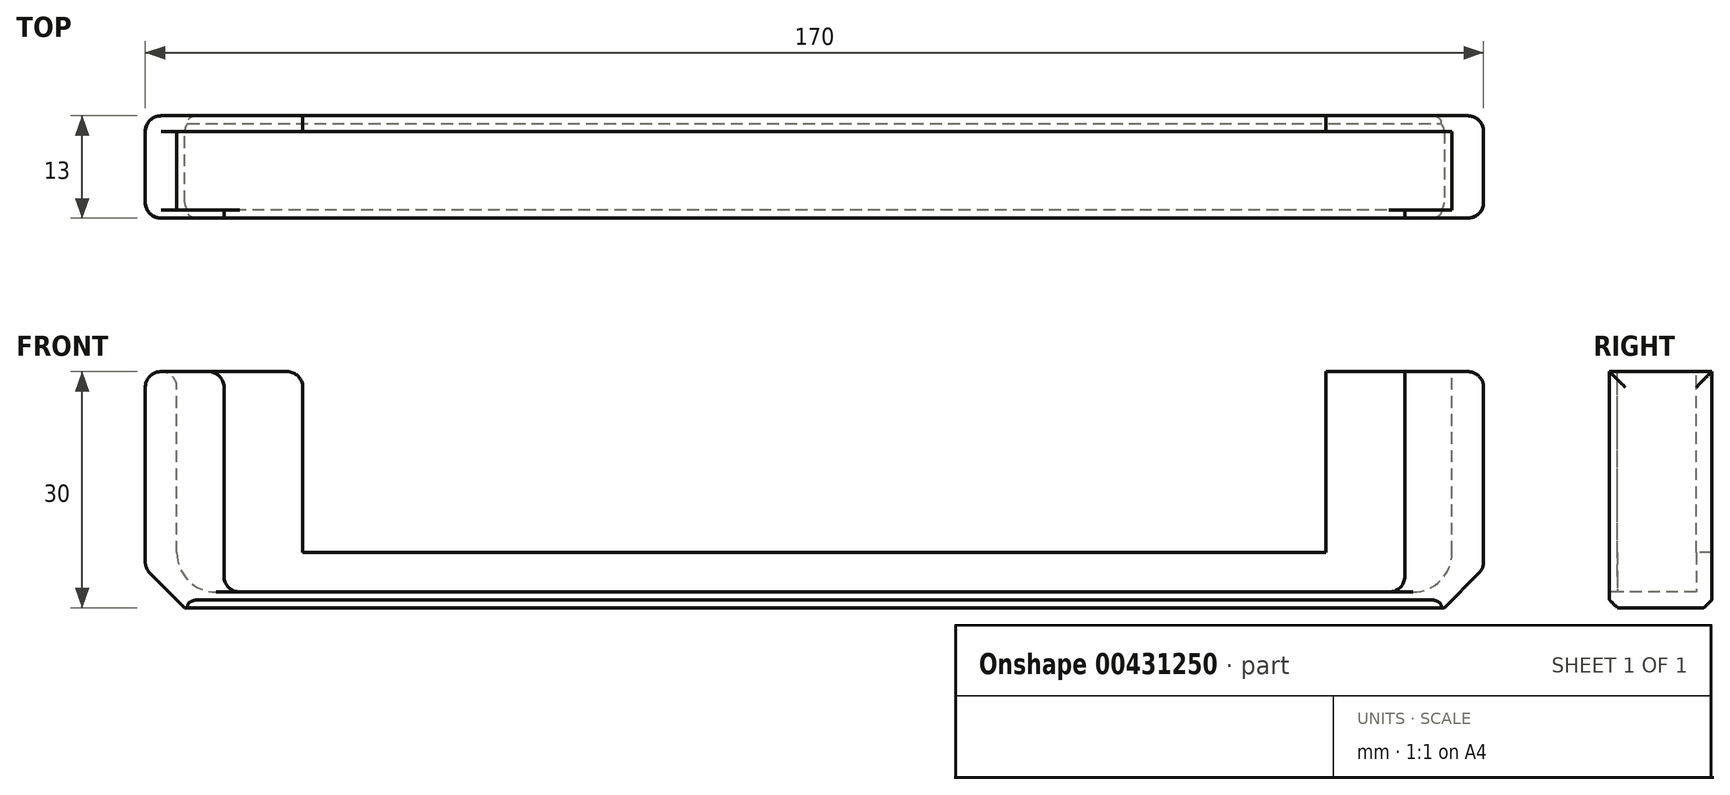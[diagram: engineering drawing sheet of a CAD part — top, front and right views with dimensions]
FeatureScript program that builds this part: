
annotation { "Feature Type Name" : "Feature", "Feature Type Description" : "" }
export const myFeature = defineFeature(function(context is Context, id is Id, definition is map)
    precondition{}
    {
        {
            var Q0;
            Q0=qCreatedBy(makeId("Front.planeOp"),FACE);
            var sketch = newSketch(context, id + "F0", { "sketchPlane" : qUnion([Q0])});
            skLineSegment(sketch, "E0.bottom", {"start": v(-85, 0) * mm, "end": v(85, 0) * mm});
            skLineSegment(sketch, "E0.top", {"start": v(-85, 30) * mm, "end": v(85, 30) * mm});
            skLineSegment(sketch, "E0.left", {"start": v(-85, 0) * mm, "end": v(-85, 30) * mm});
            skLineSegment(sketch, "E0.right", {"start": v(85, 0) * mm, "end": v(85, 30) * mm});
            skSolve(sketch);
        }
        {
            var Q0;
            Q0=qSketchRegion(id+"F0",true);
            extrude(context, id + "F1", {"entities" : qUnion([Q0]), "depth" : 13 * mm});
        }
        {
            var Q0;
            Q0=makeQuery(id+"F1.opExtrude","SWEPT_FACE",FACE,{"disambiguationData":[OSD([sQuery(id+"F0.wireOp",EDGE,"E0.top")])]});
            var sketch = newSketch(context, id + "F2", { "sketchPlane" : qUnion([Q0])});
            skLineSegment(sketch, "E1.bottom", {"start": v(-81, -2) * mm, "end": v(-65, -2) * mm});
            skLineSegment(sketch, "E1.top", {"start": v(-81, -12) * mm, "end": v(-75, -12) * mm});
            skLineSegment(sketch, "E1.left", {"start": v(-81, -2) * mm, "end": v(-81, -12) * mm});
            skLineSegment(sketch, "E1.right", {"start": v(81, -2) * mm, "end": v(81, -12) * mm});
            skLineSegment(sketch, "E2", {"start": v(-75, -12) * mm, "end": v(-75, -13) * mm});
            skLineSegment(sketch, "E3", {"start": v(-75, -13) * mm, "end": v(75, -13) * mm});
            skLineSegment(sketch, "E4", {"start": v(75, -13) * mm, "end": v(75, -12) * mm});
            skLineSegment(sketch, "E5.trimOffspring", {"start": v(75, -12) * mm, "end": v(81, -12) * mm});
            skLineSegment(sketch, "E6", {"start": v(-65, -2) * mm, "end": v(-65, 0) * mm});
            skLineSegment(sketch, "E7", {"start": v(-65, 0) * mm, "end": v(65, 0) * mm});
            skLineSegment(sketch, "E8", {"start": v(65, 0) * mm, "end": v(65, -2) * mm});
            skLineSegment(sketch, "E9.trimOffspring", {"start": v(65, -2) * mm, "end": v(81, -2) * mm});
            skSolve(sketch);
        }
        {
            var Q0;
            Q0=qSketchRegion(id+"F2",true);
            extrude(context, id + "F3", {"entities" : qUnion([Q0]), "operationType" : NewBodyOperationType.REMOVE, "oppositeDirection" : true, "depth" : 28 * mm});
        }
        {
            var Q0;
            Q0=makeQuery(id+"F3.boolean.opBoolean","COPY",FACE,{"derivedFrom":makeQuery(id+"F3.opExtrude","CAP_FACE",FACE,{"disambiguationData":[OSD([sQuery(id+"F2.wireOp",EDGE,"E1.bottom"),sQuery(id+"F2.wireOp",EDGE,"E1.top"),sQuery(id+"F2.wireOp",EDGE,"E1.left"),sQuery(id+"F2.wireOp",EDGE,"E1.right"),sQuery(id+"F2.wireOp",EDGE,"E2"),sQuery(id+"F2.wireOp",EDGE,"E3"),sQuery(id+"F2.wireOp",EDGE,"E4"),sQuery(id+"F2.wireOp",EDGE,"E5.trimOffspring"),sQuery(id+"F2.wireOp",EDGE,"E6"),sQuery(id+"F2.wireOp",EDGE,"E7"),sQuery(id+"F2.wireOp",EDGE,"E8"),sQuery(id+"F2.wireOp",EDGE,"E9.trimOffspring")])],"isStart":false})});
            var sketch = newSketch(context, id + "F4", { "sketchPlane" : qUnion([Q0])});
            skLineSegment(sketch, "E10.bottom", {"start": v(65, -2) * mm, "end": v(-65, -2) * mm});
            skLineSegment(sketch, "E10.top", {"start": v(65, 0) * mm, "end": v(-65, 0) * mm});
            skLineSegment(sketch, "E10.left", {"start": v(65, -2) * mm, "end": v(65, 0) * mm});
            skLineSegment(sketch, "E10.right", {"start": v(-65, -2) * mm, "end": v(-65, 0) * mm});
            skSolve(sketch);
        }
        {
            var Q0;
            Q0=qSketchRegion(id+"F4",true);
            extrude(context, id + "F5", {"entities" : qUnion([Q0]), "operationType" : NewBodyOperationType.ADD, "depth" : 5 * mm});
        }
        {
            var Q0;
            Q0=makeQuery(id+"F1.opExtrude","SWEPT_EDGE",EDGE,{"disambiguationData":[OSD([sQuery(id+"F0.wireOp",EDGE,"E0.bottom"),sQuery(id+"F0.wireOp",EDGE,"E0.right")])]});
            var Q1;
            Q1=makeQuery(id+"F1.opExtrude","SWEPT_EDGE",EDGE,{"disambiguationData":[OSD([sQuery(id+"F0.wireOp",EDGE,"E0.bottom"),sQuery(id+"F0.wireOp",EDGE,"E0.left")])]});
            chamfer(context, id + "F6", {"entities" : qUnion([Q0, Q1]), "width" : 5 * mm, "tangentPropagation" : true});
        }
        {
            var Q0;
            Q0=makeQuery(id+"F3.boolean.opBoolean","COPY",EDGE,{"derivedFrom":makeQuery(id+"F3.opExtrude","CAP_EDGE",EDGE,{"disambiguationData":[OSD([sQuery(id+"F2.wireOp",EDGE,"E1.left")])],"isStart":false})});
            var Q1;
            Q1=makeQuery(id+"F3.boolean.opBoolean","COPY",EDGE,{"derivedFrom":makeQuery(id+"F3.opExtrude","CAP_EDGE",EDGE,{"disambiguationData":[OSD([sQuery(id+"F2.wireOp",EDGE,"E1.right")])],"isStart":false})});
            fillet(context, id + "F7", {"entities" : qUnion([Q0, Q1]), "radius" : 5 * mm, "tangentPropagation" : true, "allowEdgeOverflow" : false});
        }
        {
            var Q0;
            Q0=makeQuery(id+"F1.opExtrude","CAP_EDGE",EDGE,{"disambiguationData":[OSD([sQuery(id+"F0.wireOp",EDGE,"E0.bottom")])],"isStart":false});
            var Q1;
            Q1=makeQuery(id+"F1.opExtrude","CAP_EDGE",EDGE,{"disambiguationData":[OSD([sQuery(id+"F0.wireOp",EDGE,"E0.bottom")])],"isStart":true});
            chamfer(context, id + "F8", {"entities" : qUnion([Q0, Q1]), "width" : 1 * mm, "tangentPropagation" : true});
        }
        {
            var Q0;
            {var subQ0=sQuery(id+"F0.wireOp",EDGE,"E0.left");Q0=makeQuery(id+"F6.opChamfer","BLEND_EDGE",EDGE,{"blendedFrom":[makeQuery(id+"F1.opExtrude","SWEPT_EDGE",EDGE,{"disambiguationData":[OSD([sQuery(id+"F0.wireOp",EDGE,"E0.bottom"),subQ0])]}),makeQuery(id+"F1.opExtrude","SWEPT_FACE",FACE,{"disambiguationData":[OSD([subQ0])]})],"blendedInto":[makeQuery(id+"F1.opExtrude","SWEPT_FACE",FACE,{"disambiguationData":[OSD([subQ0])]})]});}
            var Q1;
            Q1=makeQuery(id+"F1.opExtrude","SWEPT_EDGE",EDGE,{"disambiguationData":[OSD([sQuery(id+"F0.wireOp",EDGE,"E0.top"),sQuery(id+"F0.wireOp",EDGE,"E0.left")])]});
            var Q2;
            Q2=makeQuery(id+"F3.boolean.opBoolean","COPY",EDGE,{"derivedFrom":makeQuery(id+"F3.opExtrude","CAP_EDGE",EDGE,{"disambiguationData":[OSD([sQuery(id+"F2.wireOp",EDGE,"E1.left")])],"isStart":true})});
            var Q3;
            Q3=makeQuery(id+"F3.boolean.opBoolean","COPY",EDGE,{"derivedFrom":makeQuery(id+"F3.opExtrude","CAP_EDGE",EDGE,{"disambiguationData":[OSD([sQuery(id+"F2.wireOp",EDGE,"E1.right")])],"isStart":true})});
            var Q4;
            Q4=makeQuery(id+"F1.opExtrude","SWEPT_EDGE",EDGE,{"disambiguationData":[OSD([sQuery(id+"F0.wireOp",EDGE,"E0.top"),sQuery(id+"F0.wireOp",EDGE,"E0.right")])]});
            var Q5;
            {var subQ0=sQuery(id+"F0.wireOp",EDGE,"E0.right");Q5=makeQuery(id+"F6.opChamfer","BLEND_EDGE",EDGE,{"blendedFrom":[makeQuery(id+"F1.opExtrude","SWEPT_EDGE",EDGE,{"disambiguationData":[OSD([sQuery(id+"F0.wireOp",EDGE,"E0.bottom"),subQ0])]}),makeQuery(id+"F1.opExtrude","SWEPT_FACE",FACE,{"disambiguationData":[OSD([subQ0])]})],"blendedInto":[makeQuery(id+"F1.opExtrude","SWEPT_FACE",FACE,{"disambiguationData":[OSD([subQ0])]})]});}
            var Q6;
            Q6=makeQuery(id+"F5.opExtrude","CAP_EDGE",EDGE,{"disambiguationData":[OSD([sQuery(id+"F4.wireOp",EDGE,"E10.left")])],"isStart":false});
            var Q7;
            Q7=makeQuery(id+"F3.boolean.opBoolean","COPY",EDGE,{"derivedFrom":makeQuery(id+"F3.opExtrude","CAP_EDGE",EDGE,{"disambiguationData":[OSD([sQuery(id+"F2.wireOp",EDGE,"E8")])],"isStart":true})});
            var Q8;
            Q8=makeQuery(id+"F3.boolean.opBoolean","COPY",EDGE,{"derivedFrom":makeQuery(id+"F3.opExtrude","CAP_EDGE",EDGE,{"disambiguationData":[OSD([sQuery(id+"F2.wireOp",EDGE,"E4")])],"isStart":false})});
            var Q9;
            Q9=makeQuery(id+"F3.boolean.opBoolean","COPY",EDGE,{"derivedFrom":makeQuery(id+"F3.opExtrude","CAP_EDGE",EDGE,{"disambiguationData":[OSD([sQuery(id+"F2.wireOp",EDGE,"E4")])],"isStart":true})});
            var Q10;
            Q10=makeQuery(id+"F3.boolean.opBoolean","COPY",EDGE,{"derivedFrom":makeQuery(id+"F3.opExtrude","CAP_EDGE",EDGE,{"disambiguationData":[OSD([sQuery(id+"F2.wireOp",EDGE,"E6")])],"isStart":true})});
            var Q11;
            Q11=makeQuery(id+"F5.opExtrude","CAP_EDGE",EDGE,{"disambiguationData":[OSD([sQuery(id+"F4.wireOp",EDGE,"E10.right")])],"isStart":false});
            var Q12;
            Q12=makeQuery(id+"F3.boolean.opBoolean","COPY",EDGE,{"derivedFrom":makeQuery(id+"F3.opExtrude","CAP_EDGE",EDGE,{"disambiguationData":[OSD([sQuery(id+"F2.wireOp",EDGE,"E2")])],"isStart":false})});
            var Q13;
            Q13=makeQuery(id+"F3.boolean.opBoolean","COPY",EDGE,{"derivedFrom":makeQuery(id+"F3.opExtrude","CAP_EDGE",EDGE,{"disambiguationData":[OSD([sQuery(id+"F2.wireOp",EDGE,"E2")])],"isStart":true})});
            var Q14;
            Q14=makeQuery(id+"F1.opExtrude","CAP_EDGE",EDGE,{"disambiguationData":[OSD([sQuery(id+"F0.wireOp",EDGE,"E0.right")])],"isStart":true});
            var Q15;
            {var subQ0=sQuery(id+"F0.wireOp",EDGE,"E0.right");var subQ1=sQuery(id+"F0.wireOp",EDGE,"E0.bottom");Q15=makeQuery(id+"F6.opChamfer","BLEND_EDGE",EDGE,{"blendedFrom":[makeQuery(id+"F1.opExtrude","SWEPT_EDGE",EDGE,{"disambiguationData":[OSD([subQ1,subQ0])]}),makeQuery(id+"F5.boolean.opBoolean","MERGE",FACE,{"derivedFrom":[makeQuery(id+"F1.opExtrude","CAP_FACE",FACE,{"disambiguationData":[OSD([subQ1,sQuery(id+"F0.wireOp",EDGE,"E0.top"),sQuery(id+"F0.wireOp",EDGE,"E0.left"),subQ0])],"isStart":true}),makeQuery(id+"F5.opExtrude","SWEPT_FACE",FACE,{"disambiguationData":[OSD([sQuery(id+"F4.wireOp",EDGE,"E10.top")])]})]})],"blendedInto":[makeQuery(id+"F5.boolean.opBoolean","MERGE",FACE,{"derivedFrom":[makeQuery(id+"F1.opExtrude","CAP_FACE",FACE,{"disambiguationData":[OSD([subQ1,sQuery(id+"F0.wireOp",EDGE,"E0.top"),sQuery(id+"F0.wireOp",EDGE,"E0.left"),subQ0])],"isStart":true}),makeQuery(id+"F5.opExtrude","SWEPT_FACE",FACE,{"disambiguationData":[OSD([sQuery(id+"F4.wireOp",EDGE,"E10.top")])]})]})]});}
            var Q16;
            {var subQ0=sQuery(id+"F0.wireOp",EDGE,"E0.right");var subQ1=sQuery(id+"F0.wireOp",EDGE,"E0.bottom");Q16=makeQuery(id+"F6.opChamfer","BLEND_EDGE",EDGE,{"blendedFrom":[makeQuery(id+"F1.opExtrude","SWEPT_EDGE",EDGE,{"disambiguationData":[OSD([subQ1,subQ0])]}),makeQuery(id+"F1.opExtrude","CAP_FACE",FACE,{"disambiguationData":[OSD([subQ1,sQuery(id+"F0.wireOp",EDGE,"E0.top"),sQuery(id+"F0.wireOp",EDGE,"E0.left"),subQ0])],"isStart":false})],"blendedInto":[makeQuery(id+"F1.opExtrude","CAP_FACE",FACE,{"disambiguationData":[OSD([subQ1,sQuery(id+"F0.wireOp",EDGE,"E0.top"),sQuery(id+"F0.wireOp",EDGE,"E0.left"),subQ0])],"isStart":false})]});}
            var Q17;
            Q17=makeQuery(id+"F1.opExtrude","CAP_EDGE",EDGE,{"disambiguationData":[OSD([sQuery(id+"F0.wireOp",EDGE,"E0.right")])],"isStart":false});
            var Q18;
            Q18=makeQuery(id+"F1.opExtrude","CAP_EDGE",EDGE,{"disambiguationData":[OSD([sQuery(id+"F0.wireOp",EDGE,"E0.left")])],"isStart":true});
            var Q19;
            {var subQ0=sQuery(id+"F0.wireOp",EDGE,"E0.left");var subQ1=sQuery(id+"F0.wireOp",EDGE,"E0.bottom");Q19=makeQuery(id+"F6.opChamfer","BLEND_EDGE",EDGE,{"blendedFrom":[makeQuery(id+"F1.opExtrude","SWEPT_EDGE",EDGE,{"disambiguationData":[OSD([subQ1,subQ0])]}),makeQuery(id+"F5.boolean.opBoolean","MERGE",FACE,{"derivedFrom":[makeQuery(id+"F1.opExtrude","CAP_FACE",FACE,{"disambiguationData":[OSD([subQ1,sQuery(id+"F0.wireOp",EDGE,"E0.top"),subQ0,sQuery(id+"F0.wireOp",EDGE,"E0.right")])],"isStart":true}),makeQuery(id+"F5.opExtrude","SWEPT_FACE",FACE,{"disambiguationData":[OSD([sQuery(id+"F4.wireOp",EDGE,"E10.top")])]})]})],"blendedInto":[makeQuery(id+"F5.boolean.opBoolean","MERGE",FACE,{"derivedFrom":[makeQuery(id+"F1.opExtrude","CAP_FACE",FACE,{"disambiguationData":[OSD([subQ1,sQuery(id+"F0.wireOp",EDGE,"E0.top"),subQ0,sQuery(id+"F0.wireOp",EDGE,"E0.right")])],"isStart":true}),makeQuery(id+"F5.opExtrude","SWEPT_FACE",FACE,{"disambiguationData":[OSD([sQuery(id+"F4.wireOp",EDGE,"E10.top")])]})]})]});}
            var Q20;
            Q20=makeQuery(id+"F1.opExtrude","CAP_EDGE",EDGE,{"disambiguationData":[OSD([sQuery(id+"F0.wireOp",EDGE,"E0.left")])],"isStart":false});
            var Q21;
            {var subQ0=sQuery(id+"F0.wireOp",EDGE,"E0.left");var subQ1=sQuery(id+"F0.wireOp",EDGE,"E0.bottom");Q21=makeQuery(id+"F6.opChamfer","BLEND_EDGE",EDGE,{"blendedFrom":[makeQuery(id+"F1.opExtrude","SWEPT_EDGE",EDGE,{"disambiguationData":[OSD([subQ1,subQ0])]}),makeQuery(id+"F1.opExtrude","CAP_FACE",FACE,{"disambiguationData":[OSD([subQ1,sQuery(id+"F0.wireOp",EDGE,"E0.top"),subQ0,sQuery(id+"F0.wireOp",EDGE,"E0.right")])],"isStart":false})],"blendedInto":[makeQuery(id+"F1.opExtrude","CAP_FACE",FACE,{"disambiguationData":[OSD([subQ1,sQuery(id+"F0.wireOp",EDGE,"E0.top"),subQ0,sQuery(id+"F0.wireOp",EDGE,"E0.right")])],"isStart":false})]});}
            fillet(context, id + "F9", {"entities" : qUnion([Q0, Q1, Q2, Q3, Q4, Q5, Q6, Q7, Q8, Q9, Q10, Q11, Q12, Q13, Q14, Q15, Q16, Q17, Q18, Q19, Q20, Q21]), "radius" : 2 * mm, "tangentPropagation" : true, "allowEdgeOverflow" : false});
        }
    });
